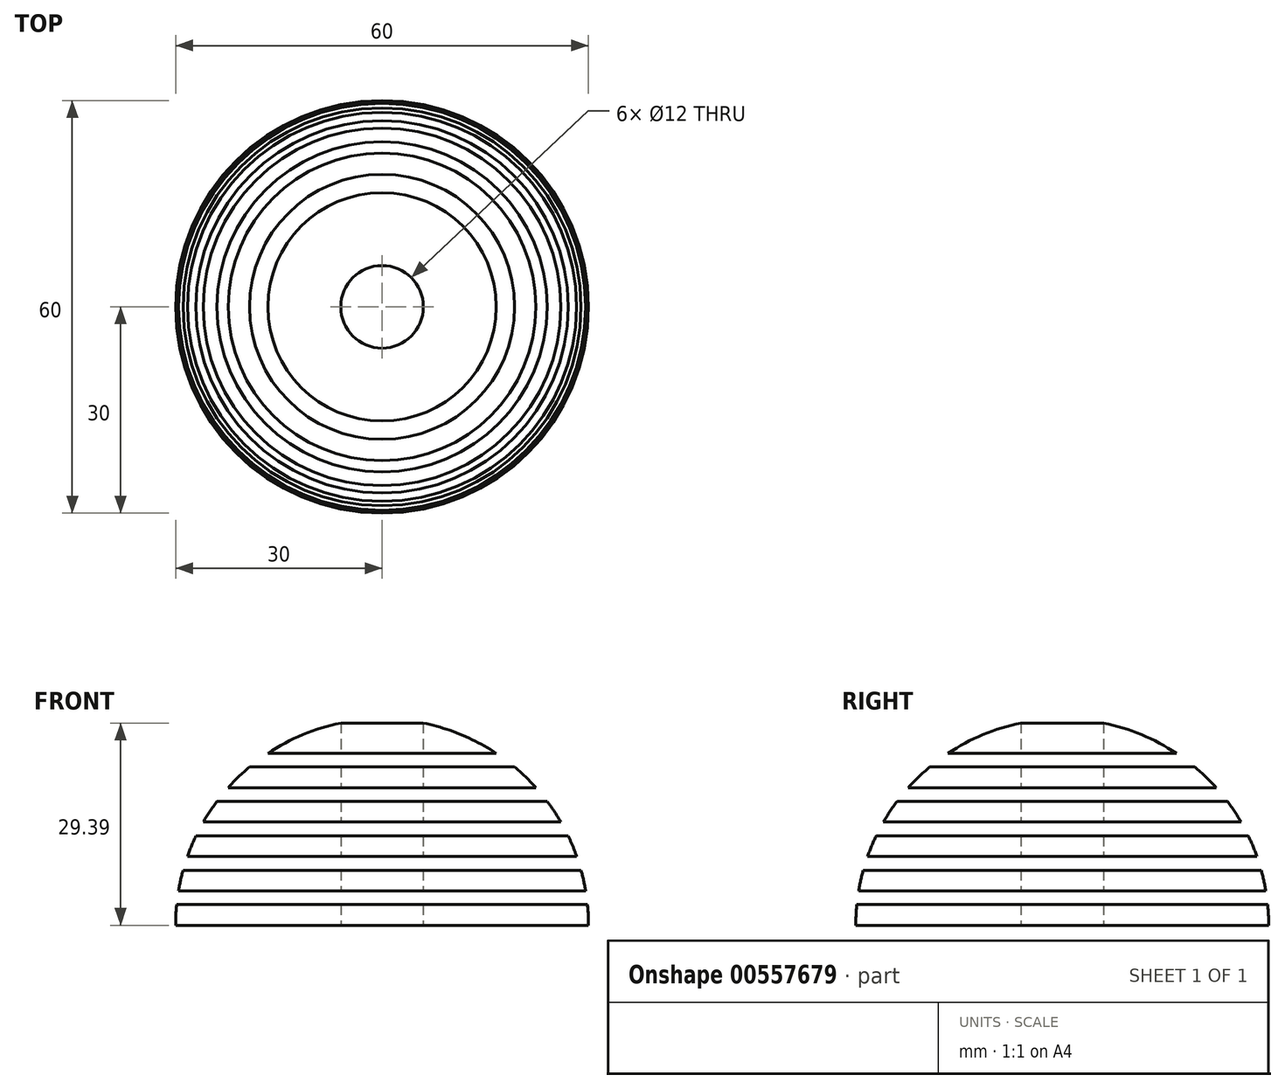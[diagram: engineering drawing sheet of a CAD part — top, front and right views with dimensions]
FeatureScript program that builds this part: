
annotation { "Feature Type Name" : "Feature", "Feature Type Description" : "" }
export const myFeature = defineFeature(function(context is Context, id is Id, definition is map)
    precondition{}
    {
        {
            var Q0;
            Q0=qCreatedBy(makeId("Front.planeOp"),FACE);
            var sketch = newSketch(context, id + "F0", { "sketchPlane" : qUnion([Q0])});
            skArc(sketch, "E0", {"start": v(30, 0) * mm, "mid": v(21.21, 21.21) * mm, "end": v(0, 30) * mm});
            skLineSegment(sketch, "E1", {"start": v(0, 0) * mm, "end": v(30, 0) * mm});
            skLineSegment(sketch, "E2", {"start": v(0, 0) * mm, "end": v(0, 30) * mm});
            skSolve(sketch);
        }
        {
            var Q0;
            Q0 = qSketchRegion(id + "F0", true);
            var Q1;
            Q1=sQuery(id+"F0.wireOp",EDGE,"E2");
            revolve(context, id + "F1", {"entities" : qUnion([Q0]), "axis" : qUnion([Q1]), "revolveType" : RevolveType.FULL});
        }
        {
            var Q0;
            Q0=qCreatedBy(makeId("Top.planeOp"),FACE);
            cPlane(context, id + "F2", {"entities" : qUnion([Q0]), "cplaneType" : CPlaneType.OFFSET, "offset" : 3 * mm, "width" : 150 * mm, "height" : 150 * mm});
        }
        {
            var Q0;
            Q0=qCreatedBy(id+"F2.planeOp",FACE);
            var sketch = newSketch(context, id + "F3", { "sketchPlane" : qUnion([Q0])});
            skCircle(sketch, "E3", {"center": v(0, 0) * mm, "radius": 38.25 * mm});
            skSolve(sketch);
        }
        {
            var Q0;
            Q0 = qSketchRegion(id + "F3", true);
            extrude(context, id + "F4", {"entities" : qUnion([Q0]), "operationType" : NewBodyOperationType.REMOVE, "depth" : 2 * mm, "offsetDistance" : 25 * mm});
        }
        {
            var Q0;
            Q0=qCreatedBy(id+"F2.planeOp",FACE);
            cPlane(context, id + "F5", {"entities" : qUnion([Q0]), "cplaneType" : CPlaneType.OFFSET, "offset" : 5 * mm, "width" : 150 * mm, "height" : 150 * mm});
        }
        {
            var Q0;
            Q0=qCreatedBy(id+"F5.planeOp",FACE);
            var sketch = newSketch(context, id + "F6", { "sketchPlane" : qUnion([Q0])});
            skCircle(sketch, "E4", {"center": v(0, 0) * mm, "radius": 37.54 * mm});
            skSolve(sketch);
        }
        {
            var Q0;
            Q0 = qSketchRegion(id + "F6", true);
            extrude(context, id + "F7", {"entities" : qUnion([Q0]), "operationType" : NewBodyOperationType.REMOVE, "depth" : 2 * mm, "offsetDistance" : 25 * mm});
        }
        {
            var Q0;
            Q0=qCreatedBy(id+"F5.planeOp",FACE);
            cPlane(context, id + "F8", {"entities" : qUnion([Q0]), "cplaneType" : CPlaneType.OFFSET, "offset" : 5 * mm, "width" : 150 * mm, "height" : 150 * mm});
        }
        {
            var Q0;
            Q0=qCreatedBy(id+"F8.planeOp",FACE);
            var sketch = newSketch(context, id + "F9", { "sketchPlane" : qUnion([Q0])});
            skCircle(sketch, "E5", {"center": v(0, 0) * mm, "radius": 34.9 * mm});
            skSolve(sketch);
        }
        {
            var Q0;
            Q0 = qSketchRegion(id + "F9", true);
            extrude(context, id + "F10", {"entities" : qUnion([Q0]), "operationType" : NewBodyOperationType.REMOVE, "depth" : 2 * mm, "offsetDistance" : 25 * mm});
        }
        {
            var Q0;
            Q0=qCreatedBy(id+"F8.planeOp",FACE);
            cPlane(context, id + "F11", {"entities" : qUnion([Q0]), "cplaneType" : CPlaneType.OFFSET, "offset" : 5 * mm, "width" : 150 * mm, "height" : 150 * mm});
        }
        {
            var Q0;
            Q0=qCreatedBy(id+"F11.planeOp",FACE);
            var sketch = newSketch(context, id + "F12", { "sketchPlane" : qUnion([Q0])});
            skCircle(sketch, "E6", {"center": v(0, 0) * mm, "radius": 35.8 * mm});
            skSolve(sketch);
        }
        {
            var Q0;
            Q0 = qSketchRegion(id + "F12", true);
            extrude(context, id + "F13", {"entities" : qUnion([Q0]), "operationType" : NewBodyOperationType.REMOVE, "depth" : 2 * mm, "offsetDistance" : 25 * mm});
        }
        {
            var Q0;
            Q0=qCreatedBy(id+"F11.planeOp",FACE);
            cPlane(context, id + "F14", {"entities" : qUnion([Q0]), "cplaneType" : CPlaneType.OFFSET, "offset" : 5 * mm, "width" : 150 * mm, "height" : 150 * mm});
        }
        {
            var Q0;
            Q0=qCreatedBy(id+"F14.planeOp",FACE);
            var sketch = newSketch(context, id + "F15", { "sketchPlane" : qUnion([Q0])});
            skCircle(sketch, "E7", {"center": v(0, 0) * mm, "radius": 35.1 * mm});
            skSolve(sketch);
        }
        {
            var Q0;
            Q0 = qSketchRegion(id + "F15", true);
            extrude(context, id + "F16", {"entities" : qUnion([Q0]), "operationType" : NewBodyOperationType.REMOVE, "depth" : 2 * mm, "offsetDistance" : 25 * mm});
        }
        {
            var Q0;
            Q0=makeQuery(id+"F1.opRevolve","SWEPT_FACE",FACE,{"disambiguationData":[OSD([sQuery(id+"F0.wireOp",EDGE,"E1")])]});
            var sketch = newSketch(context, id + "F17", { "sketchPlane" : qUnion([Q0])});
            skCircle(sketch, "E8", {"center": v(0, 0) * mm, "radius": 6 * mm});
            skSolve(sketch);
        }
        {
            var Q0;
            Q0=makeQuery(id+"F17.imprint","IMPRINT",FACE,{"disambiguationData":[TD([[makeQuery(id+"F17.imprint","IMPRINT",EDGE,{"derivedFrom":sQuery(id+"F17.wireOp",EDGE,"E8")}),1.0]])]});
            extrude(context, id + "F18", {"entities" : qUnion([Q0]), "operationType" : NewBodyOperationType.REMOVE, "endBound" : BoundingType.SYMMETRIC, "oppositeDirection" : true, "depth" : 70 * mm, "offsetDistance" : 25 * mm});
        }
    });
